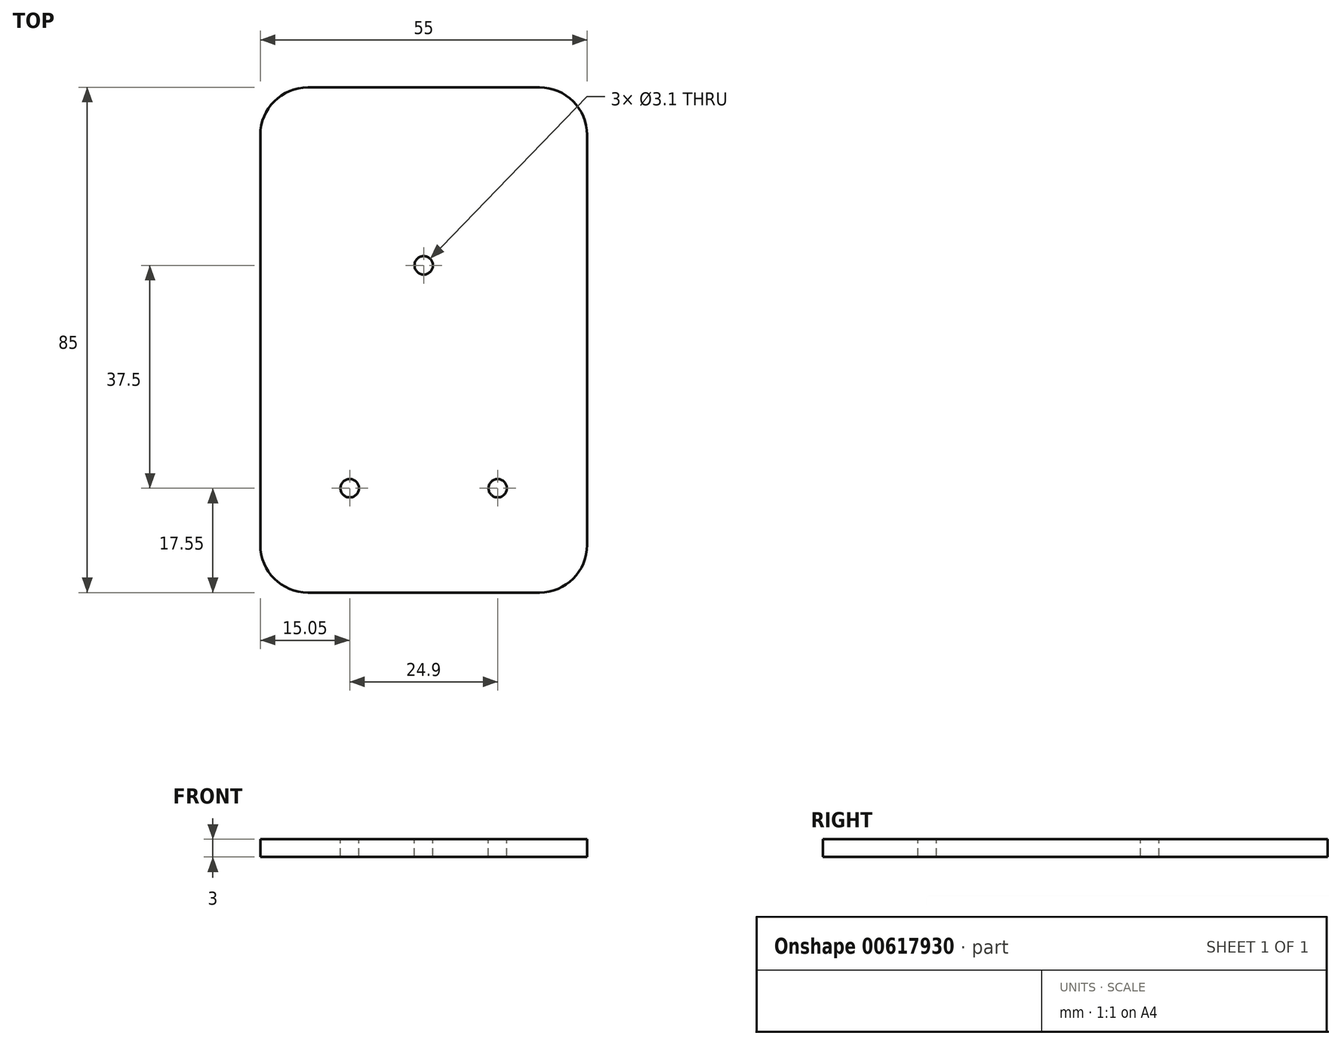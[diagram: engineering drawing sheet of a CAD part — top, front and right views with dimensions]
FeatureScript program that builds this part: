
annotation { "Feature Type Name" : "Feature", "Feature Type Description" : "" }
export const myFeature = defineFeature(function(context is Context, id is Id, definition is map)
    precondition{}
    {
        {
            var Q0;
            Q0=qCreatedBy(makeId("Top.planeOp"),FACE);
            var sketch = newSketch(context, id + "F0", { "sketchPlane" : qUnion([Q0])});
            skLineSegment(sketch, "E0.bottom", {"start": v(27.5, -42.5) * mm, "end": v(-27.5, -42.5) * mm});
            skLineSegment(sketch, "E0.top", {"start": v(27.5, 42.5) * mm, "end": v(-27.5, 42.5) * mm});
            skLineSegment(sketch, "E0.left", {"start": v(27.5, -42.5) * mm, "end": v(27.5, 42.5) * mm});
            skLineSegment(sketch, "E0.right", {"start": v(-27.5, -42.5) * mm, "end": v(-27.5, 42.5) * mm});
            skPoint(sketch, "E0.middle", {"position": v(0, 0) * mm});
            skSolve(sketch);
        }
        {
            var Q0;
            Q0 = qSketchRegion(id + "F0", true);
            extrude(context, id + "F1", {"entities" : qUnion([Q0]), "depth" : 3 * mm, "offsetDistance" : 25 * mm});
        }
        {
            var Q0;
            Q0=makeQuery(id+"F1.opExtrude","CAP_FACE",FACE,{"disambiguationData":[OSD([sQuery(id+"F0.wireOp",EDGE,"E0.bottom"),sQuery(id+"F0.wireOp",EDGE,"E0.top"),sQuery(id+"F0.wireOp",EDGE,"E0.left"),sQuery(id+"F0.wireOp",EDGE,"E0.right")])],"isStart":false});
            var sketch = newSketch(context, id + "F2", { "sketchPlane" : qUnion([Q0])});
            skLineSegment(sketch, "E1", {"start": v(0, 42.5) * mm, "end": v(0, -42.5) * mm, "construction": true});
            skLineSegment(sketch, "E2", {"start": v(-27.5, 0) * mm, "end": v(27.5, 0) * mm, "construction": true});
            skCircle(sketch, "E3", {"center": v(-12.45, -24.95) * mm, "radius": 1.55 * mm});
            skCircle(sketch, "E4", {"center": v(12.45, -24.95) * mm, "radius": 1.55 * mm});
            skCircle(sketch, "E5", {"center": v(0, 12.55) * mm, "radius": 1.55 * mm});
            skLineSegment(sketch, "E6", {"start": v(-12.45, -24.95) * mm, "end": v(12.45, -24.95) * mm, "construction": true});
            skPoint(sketch, "E7", {"position": v(0, -24.95) * mm});
            skLineSegment(sketch, "E8.bottom", {"start": v(15, -27.5) * mm, "end": v(-15, -27.5) * mm, "construction": true});
            skLineSegment(sketch, "E8.top", {"start": v(15, 15.1) * mm, "end": v(-15, 15.1) * mm, "construction": true});
            skLineSegment(sketch, "E8.left", {"start": v(15, -27.5) * mm, "end": v(15, 15.1) * mm, "construction": true});
            skLineSegment(sketch, "E8.right", {"start": v(-15, -27.5) * mm, "end": v(-15, 15.1) * mm, "construction": true});
            skPoint(sketch, "E8.middle", {"position": v(0, -6.2) * mm});
            skSolve(sketch);
        }
        {
            var Q0;
            Q0 = qSketchRegion(id + "F2", true);
            var Q1;
            Q1=makeQuery(id+"F1.opExtrude","CAP_FACE",FACE,{"disambiguationData":[OSD([sQuery(id+"F0.wireOp",EDGE,"E0.bottom"),sQuery(id+"F0.wireOp",EDGE,"E0.top"),sQuery(id+"F0.wireOp",EDGE,"E0.left"),sQuery(id+"F0.wireOp",EDGE,"E0.right")])],"isStart":true});
            extrude(context, id + "F3", {"entities" : qUnion([Q0]), "operationType" : NewBodyOperationType.REMOVE, "endBound" : BoundingType.UP_TO_SURFACE, "oppositeDirection" : true, "depth" : 25 * mm, "endBoundEntityFace" : qUnion([Q1]), "offsetDistance" : 25 * mm});
        }
        {
            var Q0;
            Q0=makeQuery(id+"F1.opExtrude","SWEPT_EDGE",EDGE,{"disambiguationData":[OSD([sQuery(id+"F0.wireOp",EDGE,"E0.bottom"),sQuery(id+"F0.wireOp",EDGE,"E0.left")])]});
            var Q1;
            Q1=makeQuery(id+"F1.opExtrude","SWEPT_EDGE",EDGE,{"disambiguationData":[OSD([sQuery(id+"F0.wireOp",EDGE,"E0.bottom"),sQuery(id+"F0.wireOp",EDGE,"E0.right")])]});
            var Q2;
            Q2=makeQuery(id+"F1.opExtrude","SWEPT_EDGE",EDGE,{"disambiguationData":[OSD([sQuery(id+"F0.wireOp",EDGE,"E0.top"),sQuery(id+"F0.wireOp",EDGE,"E0.right")])]});
            var Q3;
            Q3=makeQuery(id+"F1.opExtrude","SWEPT_EDGE",EDGE,{"disambiguationData":[OSD([sQuery(id+"F0.wireOp",EDGE,"E0.top"),sQuery(id+"F0.wireOp",EDGE,"E0.left")])]});
            fillet(context, id + "F4", {"entities" : qUnion([Q0, Q1, Q2, Q3]), "radius" : 8 * mm, "tangentPropagation" : true, "allowEdgeOverflow" : false});
        }
    });
